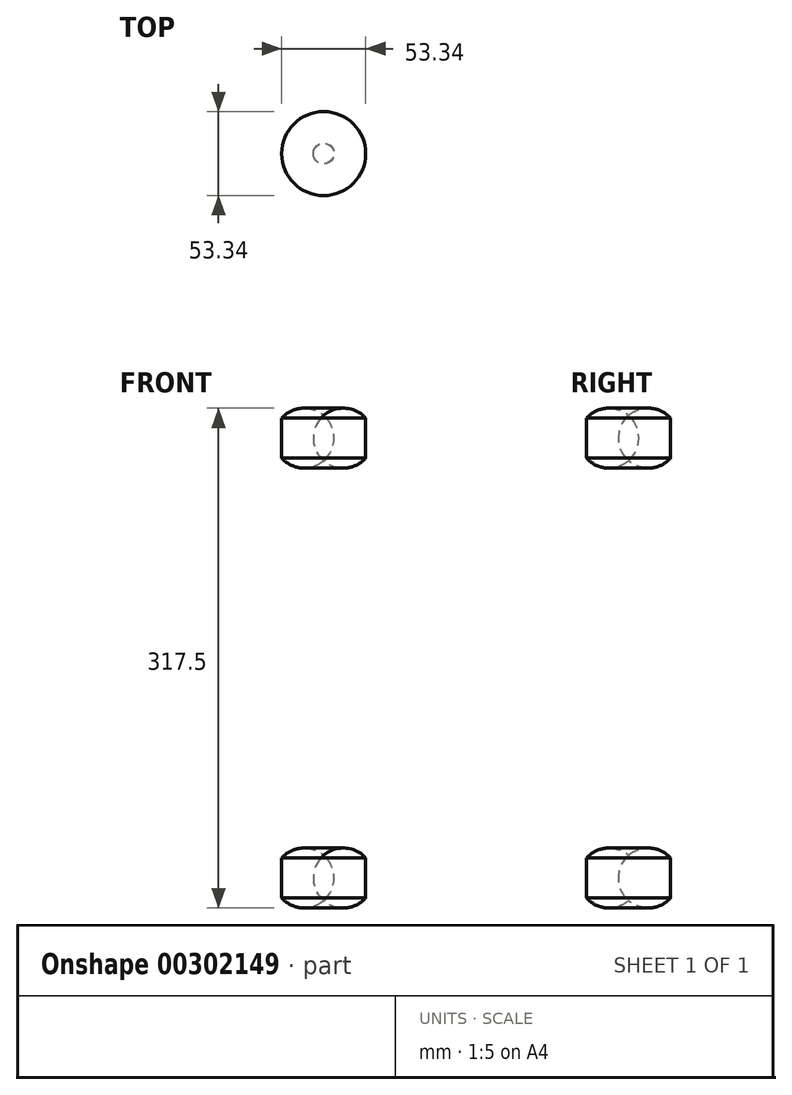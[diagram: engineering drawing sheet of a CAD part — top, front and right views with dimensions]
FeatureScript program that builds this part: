
annotation { "Feature Type Name" : "Feature", "Feature Type Description" : "" }
export const myFeature = defineFeature(function(context is Context, id is Id, definition is map)
    precondition{}
    {
        {
            var Q0;
            Q0=qCreatedBy(makeId("Front.planeOp"),FACE);
            var sketch = newSketch(context, id + "F0", { "sketchPlane" : qUnion([Q0])});
            skLineSegment(sketch, "E0", {"start": v(26.67, 246.86) * mm, "end": v(26.67, -57.94) * mm});
            skLineSegment(sketch, "E1", {"start": v(0, 246.86) * mm, "end": v(0, -57.94) * mm});
            skArc(sketch, "E2", {"start": v(26.67, 221.46) * mm, "mid": v(31.52, 234.16) * mm, "end": v(26.67, 246.86) * mm});
            skArc(sketch, "E3", {"start": v(26.67, -57.94) * mm, "mid": v(31.52, -45.24) * mm, "end": v(26.67, -32.54) * mm});
            skSolve(sketch);
        }
        {
            var Q0;
            Q0 = qSketchRegion(id + "F0", true);
            var Q1;
            Q1=sQuery(id+"F0.wireOp",EDGE,"E0");
            var Q2;
            Q2=sQuery(id+"F0.wireOp",EDGE,"E1");
            revolve(context, id + "F1", {"bodyType" : ToolBodyType.SURFACE, "entities" : qUnion([Q0]), "surfaceEntities" : qUnion([Q1]), "axis" : qUnion([Q2]), "revolveType" : RevolveType.FULL});
        }
        {
            var Q0;
            {var subQ0=sQuery(id+"F0.wireOp",EDGE,"E3");Q0=makeQuery(id+"F0.imprint","IMPRINT",FACE,{"disambiguationData":[TD([[makeQuery(id+"F0.imprint","IMPRINT",EDGE,{"derivedFrom":subQ0}),1.0]])]});}
            var Q1;
            {var subQ0=sQuery(id+"F0.wireOp",EDGE,"E2");Q1=makeQuery(id+"F0.imprint","IMPRINT",FACE,{"disambiguationData":[TD([[makeQuery(id+"F0.imprint","IMPRINT",EDGE,{"derivedFrom":subQ0}),1.0]])]});}
            var Q2;
            Q2=sQuery(id+"F0.wireOp",EDGE,"E1");
            revolve(context, id + "F2", {"entities" : qUnion([Q0, Q1]), "axis" : qUnion([Q2]), "revolveType" : RevolveType.FULL});
        }
    });
